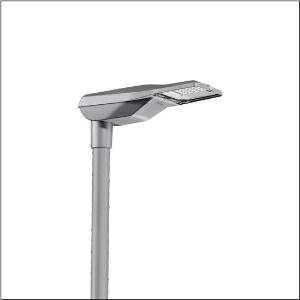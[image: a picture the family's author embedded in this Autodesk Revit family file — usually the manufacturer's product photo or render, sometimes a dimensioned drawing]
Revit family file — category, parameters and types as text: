
# Revit family: streetlight_sl_21_iq_micro___st1_0a_5xe1d41d08db_a30f
name_source: partatom
category: Lighting Fixtures
units: mm (PartAtom-declared; Revit-internal decimal feet)

## family parameters
Cut with Voids When Loaded = No
Host = Face
Light Source = No
Part Type = Normal
Room Calculation Point = No
Round Connector Dimension = Use Diameter
Shared = No

## types (1)
- --- (1 x LED, 5010 lm, 36.4 W, 4000K)
    Apparent Load = 36 VA
    CIE Flux Codes = 37 72 97 100 100
    Color Rendering = 70
    Color Temperature = 4000K
    Default Elevation = 1800 mm
    Description = Streetlight SL 21 iQ micro, mast luminaire, primary light control with lens, of PMMA, primary optical cover: cover, of toughened safety glass, transparent, light distribution: ST1.0a, light emission: direct distribution, primary light characteristic: asymmetric, installation type: post-top, side-entry, LED, High Power LED, rated luminous flux: 5.010lm, luminous efficacy: 138lm/W, light colour: 740, colour temperature: 4000K, control: Auto-Match, Temp-Guard, Lumen-Switch, Night-Set, Smart-Wire, Light-Fading, Desk-Remote (wireless, voltage-free reading and setting of iQ features in the workshop via application-optimized NFC function/RFID function), optimised constant luminous flux control (CLO 2.0), pre-setting: linear dimming characteristic, mains connection: 220..240V, AC, 50/60Hz, start of lifetime: 36W, end of service life: 38W, reduction: 16W, luminaire housing, of diecast aluminium, powder-coated, Siteco® metallic grey (DB 702S), corrosivity category C5 mid according to DIN EN ISO 12944, please order mast flange separately, inclination adjustable: 0°, 5°, 10°, 15°, sealing non-destructively replaceable, multi-level sealing system, length: 528mm, width: 235mm, height: 110mm, mast flange for spigot size: 42mm (side-entry): 5XC10008XM4, 60/48mm (side-entry/post-top): 5XC10108XM2, 76/60mm (side-entry/post-top): 5XC10108XM1, protection rating (complete): IP66, insulation class (complete): insulation class II (safety insulation), certification: CE, ENEC, ENEC+, VDE, impact resistance: IK09, permissible operating ambient temperature for outdoor applications: -40..+50°C, standard-compliant lighting for roads and squares, packaging unit: 1 piece

Light Distribution: ST1.0a
    Height = 110 mm
    Lamp = 1 x LED
    Lamp Light Flux = 5010 lm
    Lamp Power = 36.4 W
    Lamp count = 1
    Length = 528 mm
    Luminous efficacy = 138 lm/W
    Manufacturer = Siteco
    ModVariant = No
    Model = 5XE1D41D08DB
    Number of Poles = 1
    OnlyDefault = Yes
    Power Factor = 1
    Product Name = Streetlight SL 21 iQ micro | ST1.0a
    Product group = mast luminaire | pylon top
    ProductGroupID = 6100
    Protection Class = Protection class II
    Protection Degree = IP 66
    RLX_Detail_Level = 1
    RLX_Emergency_Light_Flux = 0 lm
    RLX_Emergency_Type = 0
    RLX_Emergency_Type_DB = No
    RlxData = <blob elided: 98725 chars, md5=62bf3ea6>
    Socket = socket
    Standby Power = 0 W
    System Light Flux = 5010 lm
    System Power = 36 W
    Type Comments = factory setting: luminous flux: 100 % | dim-lin: 254 | 715 mA
    Type Image = l_1006881.jpg
    URL = http://relux.com
    VarID = @adj_126321
    Voltage = 0 V
    Weight = 0.00 kg
    Width = 235 mm

## geometry (parser evidence)
native form markers: Blend x4, Sweep x10
no freeform markers — native parametric forms only
